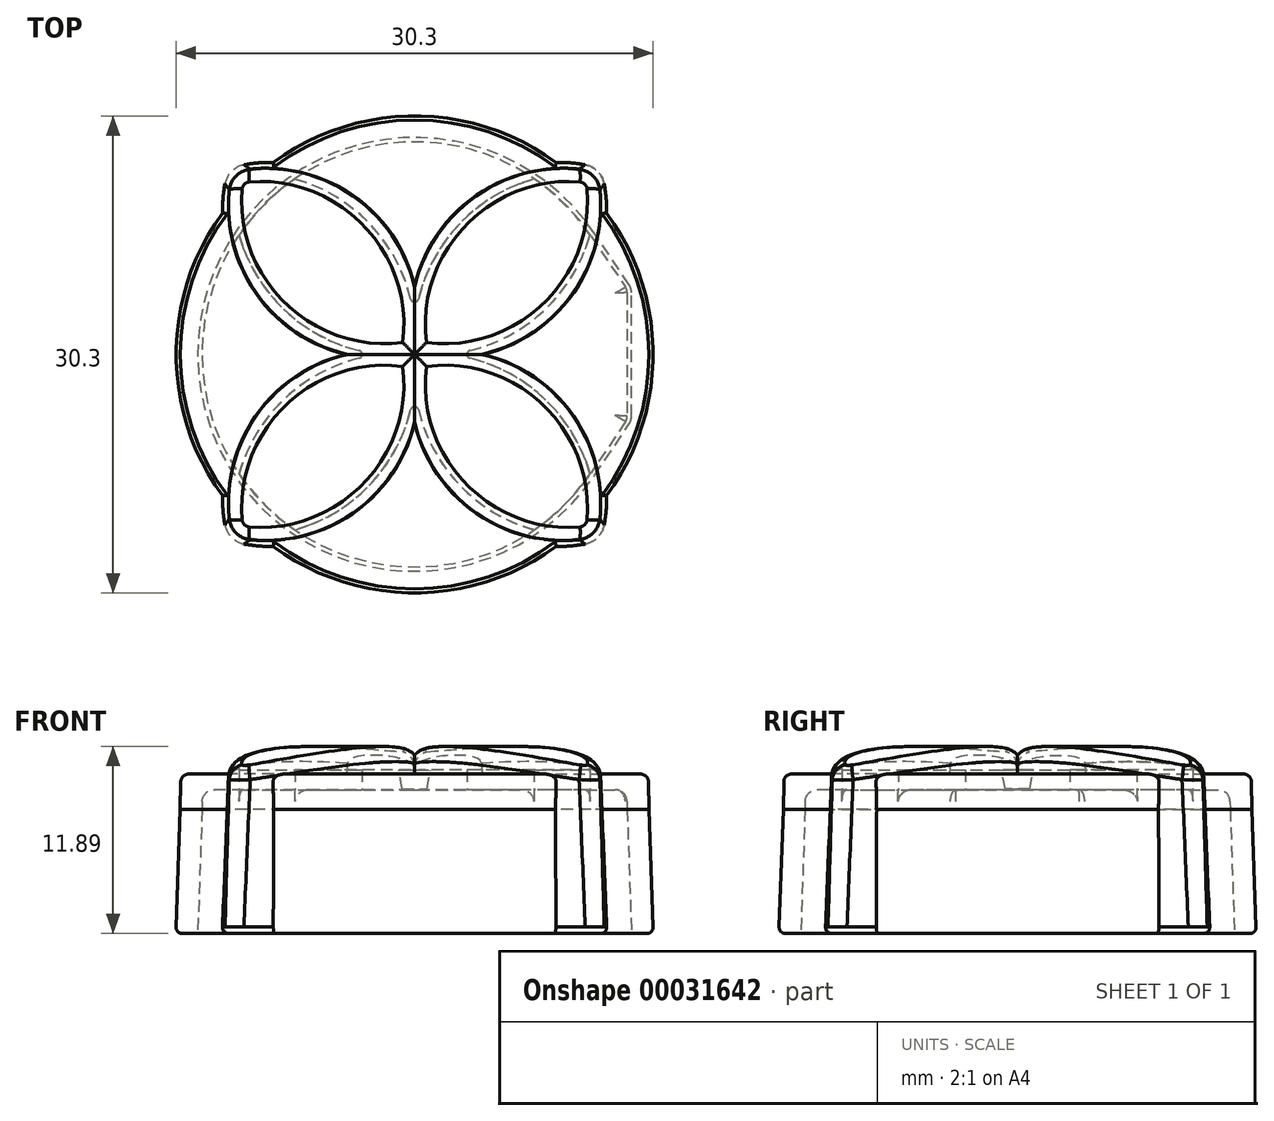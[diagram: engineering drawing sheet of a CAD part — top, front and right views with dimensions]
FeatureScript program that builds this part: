
annotation { "Feature Type Name" : "Feature", "Feature Type Description" : "" }
export const myFeature = defineFeature(function(context is Context, id is Id, definition is map)
    precondition{}
    {
        {
            var Q0;
            Q0=qCreatedBy(makeId("Top.planeOp"),FACE);
            cPlane(context, id + "F0", {"entities" : qUnion([Q0]), "cplaneType" : CPlaneType.OFFSET, "offset" : 8.73 * mm, "width" : 150 * mm, "height" : 150 * mm});
        }
        {
            var Q0;
            Q0=qCreatedBy(id+"F0.planeOp",FACE);
            var sketch = newSketch(context, id + "F1", { "sketchPlane" : qUnion([Q0])});
            skCircle(sketch, "E0", {"center": v(0, 0) * mm, "radius": 12.38 * mm});
            skCircle(sketch, "E1", {"center": v(0, 0) * mm, "radius": 13.38 * mm});
            skLineSegment(sketch, "E2.bottom", {"start": v(12.37, 4.08) * mm, "end": v(13.37, 4.08) * mm});
            skLineSegment(sketch, "E2.top", {"start": v(12.37, -4.07) * mm, "end": v(13.37, -4.07) * mm});
            skLineSegment(sketch, "E2.left", {"start": v(12.37, 3.91) * mm, "end": v(12.37, -3.91) * mm});
            skLineSegment(sketch, "E2.right", {"start": v(13.37, 3.92) * mm, "end": v(13.37, -3.92) * mm});
            skLineSegment(sketch, "E3", {"start": v(12.28, 4.2) * mm, "end": v(9.95, 7.35) * mm});
            skLineSegment(sketch, "E4", {"start": v(13.3, 4.2) * mm, "end": v(11.1, 7.46) * mm});
            skLineSegment(sketch, "E5", {"start": v(12.28, -4.2) * mm, "end": v(9.95, -7.35) * mm});
            skLineSegment(sketch, "E6", {"start": v(13.3, -4.2) * mm, "end": v(11.1, -7.46) * mm});
            skPoint(sketch, "E7.visualSharp", {"position": v(13.37, 4.08) * mm});
            skArc(sketch, "E7.filletArc", {"start": v(13.37, 3.92) * mm, "mid": v(13.35, 4.07) * mm, "end": v(13.3, 4.2) * mm});
            skPoint(sketch, "E8.visualSharp", {"position": v(13.37, -4.07) * mm});
            skArc(sketch, "E8.filletArc", {"start": v(13.3, -4.2) * mm, "mid": v(13.35, -4.07) * mm, "end": v(13.38, -3.92) * mm});
            skPoint(sketch, "E9.visualSharp", {"position": v(12.37, -4.07) * mm});
            skArc(sketch, "E9.filletArc", {"start": v(12.28, -4.2) * mm, "mid": v(12.35, -4.07) * mm, "end": v(12.38, -3.91) * mm});
            skPoint(sketch, "E10.visualSharp", {"position": v(12.37, 4.08) * mm});
            skArc(sketch, "E10.filletArc", {"start": v(12.38, 3.91) * mm, "mid": v(12.35, 4.07) * mm, "end": v(12.28, 4.2) * mm});
            skCircle(sketch, "E11.0", {"center": v(0, 0) * mm, "radius": 13.5 * mm});
            skLineSegment(sketch, "E12.0", {"start": v(13.4, 4.27) * mm, "end": v(11.2, 7.53) * mm});
            skArc(sketch, "E13.0", {"start": v(13.5, 3.92) * mm, "mid": v(13.47, 4.1) * mm, "end": v(13.4, 4.27) * mm});
            skLineSegment(sketch, "E14.0", {"start": v(13.5, 3.92) * mm, "end": v(13.5, -3.92) * mm});
            skArc(sketch, "E15.0", {"start": v(13.4, -4.27) * mm, "mid": v(13.47, -4.1) * mm, "end": v(13.5, -3.92) * mm});
            skLineSegment(sketch, "E16.0", {"start": v(13.4, -4.27) * mm, "end": v(11.2, -7.53) * mm});
            skCircle(sketch, "E17", {"center": v(0, 0) * mm, "radius": 14.88 * mm});
            skSolve(sketch);
        }
        {
            var Q0;
            {var subQ6=sQuery(id+"F1.wireOp",EDGE,"E12.0");Q0=makeQuery(id+"F1.imprint","IMPRINT",FACE,{"disambiguationData":[TD([[makeQuery(id+"F1.imprint","IMPRINT",EDGE,{"derivedFrom":subQ6}),-1.0]])]});}
            var Q1;
            {var subQ0=sQuery(id+"F1.wireOp",EDGE,"E0");var subQ3=makeQuery(id+"F1.imprint","INTERSECT",VERTEX,{"derivedFrom":[subQ0,sQuery(id+"F1.wireOp",EDGE,"E3")]});Q1=makeQuery(id+"F1.imprint","IMPRINT",FACE,{"disambiguationData":[TD([[makeQuery(id+"F1.imprint","IMPRINT",EDGE,{"disambiguationData":[TD([[subQ3,1.0]])],"derivedFrom":subQ0}),1.0]])]});}
            var Q2;
            {var subQ5=sQuery(id+"F1.wireOp",EDGE,"E4");var subQ7=sQuery(id+"F1.wireOp",EDGE,"E1");var subQ9=makeQuery(id+"F1.imprint","INTERSECT",VERTEX,{"derivedFrom":[subQ7,subQ5]});Q2=makeQuery(id+"F1.imprint","IMPRINT",FACE,{"disambiguationData":[TD([[makeQuery(id+"F1.imprint","IMPRINT",EDGE,{"disambiguationData":[TD([[subQ9,-1.0]])],"derivedFrom":subQ7}),-1.0]])]});}
            var Q3;
            {var subQ1=sQuery(id+"F1.wireOp",EDGE,"E3");Q3=makeQuery(id+"F1.imprint","IMPRINT",FACE,{"disambiguationData":[TD([[makeQuery(id+"F1.imprint","IMPRINT",EDGE,{"derivedFrom":subQ1}),-1.0]])]});}
            var Q4;
            {var subQ1=sQuery(id+"F1.wireOp",EDGE,"E3");Q4=makeQuery(id+"F1.imprint","IMPRINT",FACE,{"disambiguationData":[TD([[makeQuery(id+"F1.imprint","IMPRINT",EDGE,{"derivedFrom":subQ1}),1.0]])]});}
            var Q5;
            {var subQ3=sQuery(id+"F1.wireOp",EDGE,"E2.bottom");var subQ5=sQuery(id+"F1.wireOp",EDGE,"E7.filletArc");var subQ6=makeQuery(id+"F1.imprint","INTERSECT",VERTEX,{"derivedFrom":[subQ3,subQ5]});Q5=makeQuery(id+"F1.imprint","IMPRINT",FACE,{"disambiguationData":[TD([[makeQuery(id+"F1.imprint","IMPRINT",EDGE,{"disambiguationData":[TD([[subQ6,1.0]])],"derivedFrom":subQ3}),1.0]])]});}
            var Q6;
            {var subQ3=sQuery(id+"F1.wireOp",EDGE,"E2.bottom");var subQ5=sQuery(id+"F1.wireOp",EDGE,"E7.filletArc");var subQ6=makeQuery(id+"F1.imprint","INTERSECT",VERTEX,{"derivedFrom":[subQ3,subQ5]});Q6=makeQuery(id+"F1.imprint","IMPRINT",FACE,{"disambiguationData":[TD([[makeQuery(id+"F1.imprint","IMPRINT",EDGE,{"disambiguationData":[TD([[subQ6,1.0]])],"derivedFrom":subQ3}),-1.0]])]});}
            var Q7;
            {var subQ3=sQuery(id+"F1.wireOp",EDGE,"E2.bottom");var subQ5=sQuery(id+"F1.wireOp",EDGE,"E1");var subQ7=makeQuery(id+"F1.imprint","INTERSECT",VERTEX,{"derivedFrom":[subQ5,subQ3]});Q7=makeQuery(id+"F1.imprint","IMPRINT",FACE,{"disambiguationData":[TD([[makeQuery(id+"F1.imprint","IMPRINT",EDGE,{"disambiguationData":[TD([[subQ7,1.0]])],"derivedFrom":subQ5}),-1.0]])]});}
            var Q8;
            {var subQ1=sQuery(id+"F1.wireOp",EDGE,"E4");var subQ5=sQuery(id+"F1.wireOp",EDGE,"E1");var subQ6=makeQuery(id+"F1.imprint","INTERSECT",VERTEX,{"derivedFrom":[subQ5,subQ1]});Q8=makeQuery(id+"F1.imprint","IMPRINT",FACE,{"disambiguationData":[TD([[makeQuery(id+"F1.imprint","IMPRINT",EDGE,{"disambiguationData":[TD([[subQ6,1.0]])],"derivedFrom":subQ5}),-1.0]])]});}
            var Q9;
            {var subQ4=sQuery(id+"F1.wireOp",EDGE,"E12.0");Q9=makeQuery(id+"F1.imprint","IMPRINT",FACE,{"disambiguationData":[TD([[makeQuery(id+"F1.imprint","IMPRINT",EDGE,{"derivedFrom":subQ4}),1.0]])]});}
            var Q10;
            {var subQ2=sQuery(id+"F1.wireOp",EDGE,"E2.right");var subQ5=makeQuery(id+"F1.imprint","INTERSECT",VERTEX,{"derivedFrom":[sQuery(id+"F1.wireOp",EDGE,"E1"),subQ2]});Q10=makeQuery(id+"F1.imprint","IMPRINT",FACE,{"disambiguationData":[TD([[makeQuery(id+"F1.imprint","IMPRINT",EDGE,{"disambiguationData":[TD([[subQ5,1.0]])],"derivedFrom":subQ2}),1.0]])]});}
            var Q11;
            {var subQ1=sQuery(id+"F1.wireOp",EDGE,"E5");Q11=makeQuery(id+"F1.imprint","IMPRINT",FACE,{"disambiguationData":[TD([[makeQuery(id+"F1.imprint","IMPRINT",EDGE,{"derivedFrom":subQ1}),-1.0]])]});}
            var Q12;
            {var subQ3=sQuery(id+"F1.wireOp",EDGE,"E2.top");var subQ5=sQuery(id+"F1.wireOp",EDGE,"E8.filletArc");var subQ6=makeQuery(id+"F1.imprint","INTERSECT",VERTEX,{"derivedFrom":[subQ3,subQ5]});Q12=makeQuery(id+"F1.imprint","IMPRINT",FACE,{"disambiguationData":[TD([[makeQuery(id+"F1.imprint","IMPRINT",EDGE,{"disambiguationData":[TD([[subQ6,1.0]])],"derivedFrom":subQ3}),1.0]])]});}
            var Q13;
            {var subQ3=sQuery(id+"F1.wireOp",EDGE,"E2.top");var subQ5=sQuery(id+"F1.wireOp",EDGE,"E1");var subQ7=makeQuery(id+"F1.imprint","INTERSECT",VERTEX,{"derivedFrom":[subQ5,subQ3]});Q13=makeQuery(id+"F1.imprint","IMPRINT",FACE,{"disambiguationData":[TD([[makeQuery(id+"F1.imprint","IMPRINT",EDGE,{"disambiguationData":[TD([[subQ7,-1.0]])],"derivedFrom":subQ5}),-1.0]])]});}
            var Q14;
            {var subQ0=sQuery(id+"F1.wireOp",EDGE,"E15.0");Q14=makeQuery(id+"F1.imprint","IMPRINT",FACE,{"disambiguationData":[TD([[makeQuery(id+"F1.imprint","IMPRINT",EDGE,{"derivedFrom":subQ0}),1.0]])]});}
            var Q15;
            {var subQ1=sQuery(id+"F1.wireOp",EDGE,"E6");var subQ5=sQuery(id+"F1.wireOp",EDGE,"E1");var subQ6=makeQuery(id+"F1.imprint","INTERSECT",VERTEX,{"derivedFrom":[subQ5,subQ1]});Q15=makeQuery(id+"F1.imprint","IMPRINT",FACE,{"disambiguationData":[TD([[makeQuery(id+"F1.imprint","IMPRINT",EDGE,{"disambiguationData":[TD([[subQ6,-1.0]])],"derivedFrom":subQ5}),-1.0]])]});}
            var Q16;
            {var subQ3=sQuery(id+"F1.wireOp",EDGE,"E2.top");var subQ5=sQuery(id+"F1.wireOp",EDGE,"E8.filletArc");var subQ6=makeQuery(id+"F1.imprint","INTERSECT",VERTEX,{"derivedFrom":[subQ3,subQ5]});Q16=makeQuery(id+"F1.imprint","IMPRINT",FACE,{"disambiguationData":[TD([[makeQuery(id+"F1.imprint","IMPRINT",EDGE,{"disambiguationData":[TD([[subQ6,1.0]])],"derivedFrom":subQ3}),-1.0]])]});}
            extrude(context, id + "F2", {"entities" : qUnion([Q0, Q1, Q2, Q3, Q4, Q5, Q6, Q7, Q8, Q9, Q10, Q11, Q12, Q13, Q14, Q15, Q16]), "depth" : 2.25 * mm, "hasDraft" : true, "draftAngle" : 1 * degree, "draftPullDirection" : true});
        }
        {
            var Q0;
            {var subQ6=sQuery(id+"F1.wireOp",EDGE,"E12.0");Q0=makeQuery(id+"F1.imprint","IMPRINT",FACE,{"disambiguationData":[TD([[makeQuery(id+"F1.imprint","IMPRINT",EDGE,{"derivedFrom":subQ6}),-1.0]])]});}
            var Q1;
            {var subQ1=sQuery(id+"F1.wireOp",EDGE,"E3");Q1=makeQuery(id+"F1.imprint","IMPRINT",FACE,{"disambiguationData":[TD([[makeQuery(id+"F1.imprint","IMPRINT",EDGE,{"derivedFrom":subQ1}),-1.0]])]});}
            var Q2;
            {var subQ5=sQuery(id+"F1.wireOp",EDGE,"E4");var subQ7=sQuery(id+"F1.wireOp",EDGE,"E1");var subQ9=makeQuery(id+"F1.imprint","INTERSECT",VERTEX,{"derivedFrom":[subQ7,subQ5]});Q2=makeQuery(id+"F1.imprint","IMPRINT",FACE,{"disambiguationData":[TD([[makeQuery(id+"F1.imprint","IMPRINT",EDGE,{"disambiguationData":[TD([[subQ9,-1.0]])],"derivedFrom":subQ7}),-1.0]])]});}
            var Q3;
            {var subQ1=sQuery(id+"F1.wireOp",EDGE,"E3");Q3=makeQuery(id+"F1.imprint","IMPRINT",FACE,{"disambiguationData":[TD([[makeQuery(id+"F1.imprint","IMPRINT",EDGE,{"derivedFrom":subQ1}),1.0]])]});}
            var Q4;
            {var subQ0=sQuery(id+"F1.wireOp",EDGE,"E0");var subQ3=makeQuery(id+"F1.imprint","INTERSECT",VERTEX,{"derivedFrom":[subQ0,sQuery(id+"F1.wireOp",EDGE,"E3")]});Q4=makeQuery(id+"F1.imprint","IMPRINT",FACE,{"disambiguationData":[TD([[makeQuery(id+"F1.imprint","IMPRINT",EDGE,{"disambiguationData":[TD([[subQ3,1.0]])],"derivedFrom":subQ0}),1.0]])]});}
            var Q5;
            {var subQ1=sQuery(id+"F1.wireOp",EDGE,"E4");var subQ5=sQuery(id+"F1.wireOp",EDGE,"E1");var subQ6=makeQuery(id+"F1.imprint","INTERSECT",VERTEX,{"derivedFrom":[subQ5,subQ1]});Q5=makeQuery(id+"F1.imprint","IMPRINT",FACE,{"disambiguationData":[TD([[makeQuery(id+"F1.imprint","IMPRINT",EDGE,{"disambiguationData":[TD([[subQ6,1.0]])],"derivedFrom":subQ5}),-1.0]])]});}
            var Q6;
            {var subQ4=sQuery(id+"F1.wireOp",EDGE,"E12.0");Q6=makeQuery(id+"F1.imprint","IMPRINT",FACE,{"disambiguationData":[TD([[makeQuery(id+"F1.imprint","IMPRINT",EDGE,{"derivedFrom":subQ4}),1.0]])]});}
            var Q7;
            {var subQ3=sQuery(id+"F1.wireOp",EDGE,"E2.bottom");var subQ5=sQuery(id+"F1.wireOp",EDGE,"E7.filletArc");var subQ6=makeQuery(id+"F1.imprint","INTERSECT",VERTEX,{"derivedFrom":[subQ3,subQ5]});Q7=makeQuery(id+"F1.imprint","IMPRINT",FACE,{"disambiguationData":[TD([[makeQuery(id+"F1.imprint","IMPRINT",EDGE,{"disambiguationData":[TD([[subQ6,1.0]])],"derivedFrom":subQ3}),1.0]])]});}
            var Q8;
            {var subQ3=sQuery(id+"F1.wireOp",EDGE,"E2.bottom");var subQ5=sQuery(id+"F1.wireOp",EDGE,"E7.filletArc");var subQ6=makeQuery(id+"F1.imprint","INTERSECT",VERTEX,{"derivedFrom":[subQ3,subQ5]});Q8=makeQuery(id+"F1.imprint","IMPRINT",FACE,{"disambiguationData":[TD([[makeQuery(id+"F1.imprint","IMPRINT",EDGE,{"disambiguationData":[TD([[subQ6,1.0]])],"derivedFrom":subQ3}),-1.0]])]});}
            var Q9;
            {var subQ3=sQuery(id+"F1.wireOp",EDGE,"E2.bottom");var subQ5=sQuery(id+"F1.wireOp",EDGE,"E1");var subQ7=makeQuery(id+"F1.imprint","INTERSECT",VERTEX,{"derivedFrom":[subQ5,subQ3]});Q9=makeQuery(id+"F1.imprint","IMPRINT",FACE,{"disambiguationData":[TD([[makeQuery(id+"F1.imprint","IMPRINT",EDGE,{"disambiguationData":[TD([[subQ7,1.0]])],"derivedFrom":subQ5}),-1.0]])]});}
            var Q10;
            {var subQ2=sQuery(id+"F1.wireOp",EDGE,"E2.right");var subQ5=makeQuery(id+"F1.imprint","INTERSECT",VERTEX,{"derivedFrom":[sQuery(id+"F1.wireOp",EDGE,"E1"),subQ2]});Q10=makeQuery(id+"F1.imprint","IMPRINT",FACE,{"disambiguationData":[TD([[makeQuery(id+"F1.imprint","IMPRINT",EDGE,{"disambiguationData":[TD([[subQ5,1.0]])],"derivedFrom":subQ2}),1.0]])]});}
            var Q11;
            {var subQ1=sQuery(id+"F1.wireOp",EDGE,"E5");Q11=makeQuery(id+"F1.imprint","IMPRINT",FACE,{"disambiguationData":[TD([[makeQuery(id+"F1.imprint","IMPRINT",EDGE,{"derivedFrom":subQ1}),-1.0]])]});}
            var Q12;
            {var subQ3=sQuery(id+"F1.wireOp",EDGE,"E2.top");var subQ5=sQuery(id+"F1.wireOp",EDGE,"E8.filletArc");var subQ6=makeQuery(id+"F1.imprint","INTERSECT",VERTEX,{"derivedFrom":[subQ3,subQ5]});Q12=makeQuery(id+"F1.imprint","IMPRINT",FACE,{"disambiguationData":[TD([[makeQuery(id+"F1.imprint","IMPRINT",EDGE,{"disambiguationData":[TD([[subQ6,1.0]])],"derivedFrom":subQ3}),1.0]])]});}
            var Q13;
            {var subQ3=sQuery(id+"F1.wireOp",EDGE,"E2.top");var subQ5=sQuery(id+"F1.wireOp",EDGE,"E1");var subQ7=makeQuery(id+"F1.imprint","INTERSECT",VERTEX,{"derivedFrom":[subQ5,subQ3]});Q13=makeQuery(id+"F1.imprint","IMPRINT",FACE,{"disambiguationData":[TD([[makeQuery(id+"F1.imprint","IMPRINT",EDGE,{"disambiguationData":[TD([[subQ7,-1.0]])],"derivedFrom":subQ5}),-1.0]])]});}
            var Q14;
            {var subQ0=sQuery(id+"F1.wireOp",EDGE,"E15.0");Q14=makeQuery(id+"F1.imprint","IMPRINT",FACE,{"disambiguationData":[TD([[makeQuery(id+"F1.imprint","IMPRINT",EDGE,{"derivedFrom":subQ0}),1.0]])]});}
            var Q15;
            {var subQ3=sQuery(id+"F1.wireOp",EDGE,"E2.top");var subQ5=sQuery(id+"F1.wireOp",EDGE,"E8.filletArc");var subQ6=makeQuery(id+"F1.imprint","INTERSECT",VERTEX,{"derivedFrom":[subQ3,subQ5]});Q15=makeQuery(id+"F1.imprint","IMPRINT",FACE,{"disambiguationData":[TD([[makeQuery(id+"F1.imprint","IMPRINT",EDGE,{"disambiguationData":[TD([[subQ6,1.0]])],"derivedFrom":subQ3}),-1.0]])]});}
            var Q16;
            {var subQ1=sQuery(id+"F1.wireOp",EDGE,"E6");var subQ5=sQuery(id+"F1.wireOp",EDGE,"E1");var subQ6=makeQuery(id+"F1.imprint","INTERSECT",VERTEX,{"derivedFrom":[subQ5,subQ1]});Q16=makeQuery(id+"F1.imprint","IMPRINT",FACE,{"disambiguationData":[TD([[makeQuery(id+"F1.imprint","IMPRINT",EDGE,{"disambiguationData":[TD([[subQ6,-1.0]])],"derivedFrom":subQ5}),-1.0]])]});}
            extrude(context, id + "F3", {"entities" : qUnion([Q0, Q1, Q2, Q3, Q4, Q5, Q6, Q7, Q8, Q9, Q10, Q11, Q12, Q13, Q14, Q15, Q16]), "operationType" : NewBodyOperationType.ADD, "oppositeDirection" : true, "depth" : 7.88 * mm, "hasDraft" : true, "draftAngle" : 2 * degree});
        }
        {
            var Q0;
            Q0=qCreatedBy(makeId("Top.planeOp"),FACE);
            var sketch = newSketch(context, id + "F4", { "sketchPlane" : qUnion([Q0])});
            skLineSegment(sketch, "E18", {"start": v(0, 0) * mm, "end": v(0, 19.92) * mm, "construction": true});
            skLineSegment(sketch, "E19", {"start": v(0, 0) * mm, "end": v(17.2, 17.2) * mm, "construction": true});
            skArc(sketch, "E20", {"start": v(11.84, 11.84) * mm, "mid": v(2.38, 9.47) * mm, "end": v(0, 0) * mm});
            skArc(sketch, "E21.0.MirrorCS", {"start": v(11.84, 11.84) * mm, "mid": v(9.47, 2.38) * mm, "end": v(0, 0) * mm});
            skPoint(sketch, "E22.center", {"position": v(0, 0) * mm});
            skLineSegment(sketch, "E22.anchor1", {"start": v(0, 0) * mm, "end": v(0, 0) * mm});
            skLineSegment(sketch, "E22.anchor2", {"start": v(0, 0) * mm, "end": v(21.18, 0) * mm, "construction": true});
            skSolve(sketch);
        }
        {
            var Q0;
            Q0=qCreatedBy(makeId("Top.planeOp"),FACE);
            cPlane(context, id + "F5", {"entities" : qUnion([Q0]), "cplaneType" : CPlaneType.OFFSET, "offset" : 13.98 * mm, "width" : 150 * mm, "height" : 150 * mm});
        }
        {
            var Q0;
            Q0=qCreatedBy(id+"F5.planeOp",FACE);
            var sketch = newSketch(context, id + "F6", { "sketchPlane" : qUnion([Q0])});
            skLineSegment(sketch, "E23", {"start": v(0, 0) * mm, "end": v(0, 1.45) * mm, "construction": true});
            skLineSegment(sketch, "E24", {"start": v(0, 0) * mm, "end": v(22.98, 22.98) * mm, "construction": true});
            skArc(sketch, "E25", {"start": v(11.5, 11.5) * mm, "mid": v(2.63, 8.86) * mm, "end": v(0, 0) * mm});
            skArc(sketch, "E26", {"start": v(11.84, 11.84) * mm, "mid": v(2.71, 9.13) * mm, "end": v(0, 0) * mm, "construction": true});
            skArc(sketch, "E27.0.MirrorCS", {"start": v(11.5, 11.5) * mm, "mid": v(8.86, 2.63) * mm, "end": v(0, 0) * mm});
            skSolve(sketch);
        }
        {
            var Q1;
            Q1=makeQuery(id+"F4.imprint","IMPRINT",FACE,{"disambiguationData":[TD([[makeQuery(id+"F4.imprint","IMPRINT",EDGE,{"derivedFrom":sQuery(id+"F4.wireOp",EDGE,"E20")}),1.0]])]});
            var Q2;
            Q2=makeQuery(id+"F6.imprint","IMPRINT",FACE,{"disambiguationData":[TD([[makeQuery(id+"F6.imprint","IMPRINT",EDGE,{"derivedFrom":sQuery(id+"F6.wireOp",EDGE,"E25")}),1.0]])]});
            loft(context, id + "F7", {"sheetProfilesArray" : [{ "sheetProfileEntities" : qUnion([Q1]) }, { "sheetProfileEntities" : qUnion([Q2]) }]});
        }
        {
            var Q0;
            Q0=qCreatedBy(makeId("Front.planeOp"),FACE);
            var Q1;
            Q1=qCreatedBy(makeId("Right.planeOp"),FACE);
            cPlane(context, id + "F8", {"entities" : qUnion([Q0, Q1]), "cplaneType" : CPlaneType.MID_PLANE, "offset" : 150 * mm, "flipAlignment" : true, "width" : 150 * mm, "height" : 150 * mm});
        }
        {
            var Q0;
            Q0=qCreatedBy(id+"F8.planeOp",FACE);
            var sketch = newSketch(context, id + "F9", { "sketchPlane" : qUnion([Q0])});
            skLineSegment(sketch, "E28", {"start": v(0, 0) * mm, "end": v(0, 14) * mm});
            skLineSegment(sketch, "E29", {"start": v(0, 0.85) * mm, "end": v(16.75, 0.85) * mm});
            skLineSegment(sketch, "E30", {"start": v(0, 11.23) * mm, "end": v(23.83, 11.23) * mm, "construction": true});
            skLineSegment(sketch, "E31", {"start": v(16.75, 0.85) * mm, "end": v(16.37, 11.24) * mm});
            skLineSegment(sketch, "E32", {"start": v(16.75, 0.85) * mm, "end": v(16.75, 14) * mm});
            skLineSegment(sketch, "E33", {"start": v(0, 14) * mm, "end": v(16.75, 14) * mm});
            skLineSegment(sketch, "E34", {"start": v(16.75, 0.85) * mm, "end": v(16.75, -1.44) * mm});
            skLineSegment(sketch, "E35", {"start": v(16.75, -1.44) * mm, "end": v(0, -1.44) * mm});
            skLineSegment(sketch, "E36", {"start": v(0, -1.44) * mm, "end": v(0, 0.85) * mm});
            skArc(sketch, "E37", {"start": v(16.38, 11.24) * mm, "mid": v(8.24, 12.67) * mm, "end": v(0, 12.23) * mm});
            skLineSegment(sketch, "E38", {"start": v(0, 12.73) * mm, "end": v(27.33, 12.73) * mm, "construction": true});
            skSolve(sketch);
        }
        {
            var Q0;
            Q0=makeQuery(id+"F9.imprint","IMPRINT",FACE,{"disambiguationData":[TD([[makeQuery(id+"F9.imprint","IMPRINT",EDGE,{"derivedFrom":sQuery(id+"F9.wireOp",EDGE,"E31")}),-1.0]])]});
            var Q1;
            {var subQ2=sQuery(id+"F9.wireOp",EDGE,"E29");Q1=makeQuery(id+"F9.imprint","IMPRINT",FACE,{"disambiguationData":[TD([[makeQuery(id+"F9.imprint","IMPRINT",EDGE,{"derivedFrom":subQ2}),-1.0]])]});}
            extrude(context, id + "F10", {"entities" : qUnion([Q0, Q1]), "operationType" : NewBodyOperationType.REMOVE, "endBound" : BoundingType.SYMMETRIC, "oppositeDirection" : true, "depth" : 12 * mm});
        }
        {
            var Q0;
            {var subQ0=sQuery(id+"F4.wireOp",EDGE,"E20");var subQ1=sQuery(id+"F4.wireOp",EDGE,"E21.0.MirrorCS");var subQ2=sQuery(id+"F6.wireOp",EDGE,"E25");var subQ3=sQuery(id+"F6.wireOp",EDGE,"E27.0.MirrorCS");Q0=makeQuery(id+"F7.opLoft","SWEPT_EDGE",EDGE,{"disambiguationData":[OSD([subQ0,subQ1,subQ2,subQ3]),TDD([makeQuery(id+"F4.imprint","INTERSECT",VERTEX,{"disambiguationData":[OD(0.0)],"derivedFrom":[subQ0,subQ1]}),makeQuery(id+"F6.imprint","INTERSECT",VERTEX,{"disambiguationData":[OD(0.0)],"derivedFrom":[subQ2,subQ3]})])]});}
            fillet(context, id + "F11", {"entities" : qUnion([Q0]), "radius" : 1.5 * mm, "tangentPropagation" : true, "allowEdgeOverflow" : false});
        }
        {
            var Q0;
            {var subQ0=sQuery(id+"F4.wireOp",EDGE,"E20");var subQ1=sQuery(id+"F4.wireOp",EDGE,"E21.0.MirrorCS");var subQ2=sQuery(id+"F6.wireOp",EDGE,"E25");var subQ3=sQuery(id+"F6.wireOp",EDGE,"E27.0.MirrorCS");Q0=makeQuery(id+"F10.boolean.opBoolean","INTERSECT",EDGE,{"derivedFrom":[makeQuery(id+"F7.opLoft","SWEPT_FACE",FACE,{"disambiguationData":[OSD([subQ0,subQ1,subQ2,subQ3]),TDD([makeQuery(id+"F4.imprint","INTERSECT",VERTEX,{"disambiguationData":[OD(0.0)],"derivedFrom":[subQ0,subQ1]}),makeQuery(id+"F4.imprint","INTERSECT",VERTEX,{"disambiguationData":[OD(1.0)],"derivedFrom":[subQ0,subQ1]}),makeQuery(id+"F4.imprint","IMPRINT",EDGE,{"derivedFrom":subQ1}),makeQuery(id+"F6.imprint","INTERSECT",VERTEX,{"disambiguationData":[OD(0.0)],"derivedFrom":[subQ2,subQ3]}),makeQuery(id+"F6.imprint","INTERSECT",VERTEX,{"disambiguationData":[OD(1.0)],"derivedFrom":[subQ2,subQ3]}),makeQuery(id+"F6.imprint","IMPRINT",EDGE,{"derivedFrom":subQ3})])]}),makeQuery(id+"F10.opExtrude","SWEPT_FACE",FACE,{"disambiguationData":[OSD([sQuery(id+"F9.wireOp",EDGE,"E37")])]})]});}
            fillet(context, id + "F12", {"entities" : qUnion([Q0]), "radius" : 1 * mm, "tangentPropagation" : true, "allowEdgeOverflow" : false});
        }
        {
            var Q0;
            Q0=makeQuery(id+"F7.opLoft","SWEPT_BODY",BODY,{"disambiguationData":[OSD([makeQuery(id+"F4.imprint","IMPRINT",FACE,{"disambiguationData":[TD([[makeQuery(id+"F4.imprint","IMPRINT",EDGE,{"derivedFrom":sQuery(id+"F4.wireOp",EDGE,"E20")}),1.0]])]}),makeQuery(id+"F6.imprint","IMPRINT",FACE,{"disambiguationData":[TD([[makeQuery(id+"F6.imprint","IMPRINT",EDGE,{"derivedFrom":sQuery(id+"F6.wireOp",EDGE,"E25")}),1.0]])]})])]});
            var Q1;
            Q1=sQuery(id+"F9.wireOp",EDGE,"E28");
            circularPattern(context, id + "F13", {"operationType" : NewBodyOperationType.ADD, "entities" : qUnion([Q0]), "axis" : qUnion([Q1]), "angle" : 90 * degree, "instanceCount" : round(4)});
        }
        {
            var Q0;
            {var subQ0=sQuery(id+"F1.wireOp",EDGE,"E0");var subQ3=makeQuery(id+"F1.imprint","INTERSECT",VERTEX,{"derivedFrom":[subQ0,sQuery(id+"F1.wireOp",EDGE,"E3")]});Q0=makeQuery(id+"F1.imprint","IMPRINT",FACE,{"disambiguationData":[TD([[makeQuery(id+"F1.imprint","IMPRINT",EDGE,{"disambiguationData":[TD([[subQ3,1.0]])],"derivedFrom":subQ0}),1.0]])]});}
            var Q1;
            {var subQ1=sQuery(id+"F1.wireOp",EDGE,"E3");Q1=makeQuery(id+"F1.imprint","IMPRINT",FACE,{"disambiguationData":[TD([[makeQuery(id+"F1.imprint","IMPRINT",EDGE,{"derivedFrom":subQ1}),-1.0]])]});}
            var Q2;
            {var subQ5=sQuery(id+"F1.wireOp",EDGE,"E4");var subQ7=sQuery(id+"F1.wireOp",EDGE,"E1");var subQ9=makeQuery(id+"F1.imprint","INTERSECT",VERTEX,{"derivedFrom":[subQ7,subQ5]});Q2=makeQuery(id+"F1.imprint","IMPRINT",FACE,{"disambiguationData":[TD([[makeQuery(id+"F1.imprint","IMPRINT",EDGE,{"disambiguationData":[TD([[subQ9,-1.0]])],"derivedFrom":subQ7}),-1.0]])]});}
            var Q3;
            {var subQ4=sQuery(id+"F1.wireOp",EDGE,"E12.0");Q3=makeQuery(id+"F1.imprint","IMPRINT",FACE,{"disambiguationData":[TD([[makeQuery(id+"F1.imprint","IMPRINT",EDGE,{"derivedFrom":subQ4}),1.0]])]});}
            var Q4;
            {var subQ3=sQuery(id+"F1.wireOp",EDGE,"E2.bottom");var subQ5=sQuery(id+"F1.wireOp",EDGE,"E7.filletArc");var subQ6=makeQuery(id+"F1.imprint","INTERSECT",VERTEX,{"derivedFrom":[subQ3,subQ5]});Q4=makeQuery(id+"F1.imprint","IMPRINT",FACE,{"disambiguationData":[TD([[makeQuery(id+"F1.imprint","IMPRINT",EDGE,{"disambiguationData":[TD([[subQ6,1.0]])],"derivedFrom":subQ3}),1.0]])]});}
            var Q5;
            {var subQ3=sQuery(id+"F1.wireOp",EDGE,"E2.bottom");var subQ5=sQuery(id+"F1.wireOp",EDGE,"E7.filletArc");var subQ6=makeQuery(id+"F1.imprint","INTERSECT",VERTEX,{"derivedFrom":[subQ3,subQ5]});Q5=makeQuery(id+"F1.imprint","IMPRINT",FACE,{"disambiguationData":[TD([[makeQuery(id+"F1.imprint","IMPRINT",EDGE,{"disambiguationData":[TD([[subQ6,1.0]])],"derivedFrom":subQ3}),-1.0]])]});}
            var Q6;
            {var subQ1=sQuery(id+"F1.wireOp",EDGE,"E3");Q6=makeQuery(id+"F1.imprint","IMPRINT",FACE,{"disambiguationData":[TD([[makeQuery(id+"F1.imprint","IMPRINT",EDGE,{"derivedFrom":subQ1}),1.0]])]});}
            var Q7;
            {var subQ3=sQuery(id+"F1.wireOp",EDGE,"E2.bottom");var subQ5=sQuery(id+"F1.wireOp",EDGE,"E1");var subQ7=makeQuery(id+"F1.imprint","INTERSECT",VERTEX,{"derivedFrom":[subQ5,subQ3]});Q7=makeQuery(id+"F1.imprint","IMPRINT",FACE,{"disambiguationData":[TD([[makeQuery(id+"F1.imprint","IMPRINT",EDGE,{"disambiguationData":[TD([[subQ7,1.0]])],"derivedFrom":subQ5}),-1.0]])]});}
            var Q8;
            {var subQ1=sQuery(id+"F1.wireOp",EDGE,"E4");var subQ5=sQuery(id+"F1.wireOp",EDGE,"E1");var subQ6=makeQuery(id+"F1.imprint","INTERSECT",VERTEX,{"derivedFrom":[subQ5,subQ1]});Q8=makeQuery(id+"F1.imprint","IMPRINT",FACE,{"disambiguationData":[TD([[makeQuery(id+"F1.imprint","IMPRINT",EDGE,{"disambiguationData":[TD([[subQ6,1.0]])],"derivedFrom":subQ5}),-1.0]])]});}
            var Q9;
            {var subQ1=sQuery(id+"F1.wireOp",EDGE,"E5");Q9=makeQuery(id+"F1.imprint","IMPRINT",FACE,{"disambiguationData":[TD([[makeQuery(id+"F1.imprint","IMPRINT",EDGE,{"derivedFrom":subQ1}),-1.0]])]});}
            var Q10;
            {var subQ3=sQuery(id+"F1.wireOp",EDGE,"E2.top");var subQ5=sQuery(id+"F1.wireOp",EDGE,"E1");var subQ7=makeQuery(id+"F1.imprint","INTERSECT",VERTEX,{"derivedFrom":[subQ5,subQ3]});Q10=makeQuery(id+"F1.imprint","IMPRINT",FACE,{"disambiguationData":[TD([[makeQuery(id+"F1.imprint","IMPRINT",EDGE,{"disambiguationData":[TD([[subQ7,-1.0]])],"derivedFrom":subQ5}),-1.0]])]});}
            var Q11;
            {var subQ1=sQuery(id+"F1.wireOp",EDGE,"E6");var subQ5=sQuery(id+"F1.wireOp",EDGE,"E1");var subQ6=makeQuery(id+"F1.imprint","INTERSECT",VERTEX,{"derivedFrom":[subQ5,subQ1]});Q11=makeQuery(id+"F1.imprint","IMPRINT",FACE,{"disambiguationData":[TD([[makeQuery(id+"F1.imprint","IMPRINT",EDGE,{"disambiguationData":[TD([[subQ6,-1.0]])],"derivedFrom":subQ5}),-1.0]])]});}
            var Q12;
            {var subQ3=sQuery(id+"F1.wireOp",EDGE,"E2.top");var subQ5=sQuery(id+"F1.wireOp",EDGE,"E8.filletArc");var subQ6=makeQuery(id+"F1.imprint","INTERSECT",VERTEX,{"derivedFrom":[subQ3,subQ5]});Q12=makeQuery(id+"F1.imprint","IMPRINT",FACE,{"disambiguationData":[TD([[makeQuery(id+"F1.imprint","IMPRINT",EDGE,{"disambiguationData":[TD([[subQ6,1.0]])],"derivedFrom":subQ3}),-1.0]])]});}
            var Q13;
            {var subQ0=sQuery(id+"F1.wireOp",EDGE,"E15.0");Q13=makeQuery(id+"F1.imprint","IMPRINT",FACE,{"disambiguationData":[TD([[makeQuery(id+"F1.imprint","IMPRINT",EDGE,{"derivedFrom":subQ0}),1.0]])]});}
            var Q14;
            {var subQ3=sQuery(id+"F1.wireOp",EDGE,"E2.top");var subQ5=sQuery(id+"F1.wireOp",EDGE,"E8.filletArc");var subQ6=makeQuery(id+"F1.imprint","INTERSECT",VERTEX,{"derivedFrom":[subQ3,subQ5]});Q14=makeQuery(id+"F1.imprint","IMPRINT",FACE,{"disambiguationData":[TD([[makeQuery(id+"F1.imprint","IMPRINT",EDGE,{"disambiguationData":[TD([[subQ6,1.0]])],"derivedFrom":subQ3}),1.0]])]});}
            var Q15;
            {var subQ2=sQuery(id+"F1.wireOp",EDGE,"E2.right");var subQ5=makeQuery(id+"F1.imprint","INTERSECT",VERTEX,{"derivedFrom":[sQuery(id+"F1.wireOp",EDGE,"E1"),subQ2]});Q15=makeQuery(id+"F1.imprint","IMPRINT",FACE,{"disambiguationData":[TD([[makeQuery(id+"F1.imprint","IMPRINT",EDGE,{"disambiguationData":[TD([[subQ5,1.0]])],"derivedFrom":subQ2}),1.0]])]});}
            extrude(context, id + "F14", {"entities" : qUnion([Q0, Q1, Q2, Q3, Q4, Q5, Q6, Q7, Q8, Q9, Q10, Q11, Q12, Q13, Q14, Q15]), "operationType" : NewBodyOperationType.REMOVE, "depth" : 1.25 * mm, "hasDraft" : true, "draftAngle" : 1 * degree, "draftPullDirection" : true, "hasSecondDirection" : true, "secondDirectionBound" : SecondDirectionBoundingType.THROUGH_ALL, "secondDirectionOppositeDirection" : true, "secondDirectionDepth" : 25 * mm, "hasSecondDirectionDraft" : true, "secondDirectionDraftAngle" : 2 * degree});
        }
        {
            var Q0;
            Q0=makeQuery(id+"F14.boolean.opBoolean","COPY",FACE,{"disambiguationData":[OD(0.0)],"derivedFrom":makeQuery(id+"F14.opExtrude","CAP_FACE",FACE,{"disambiguationData":[OSD([sQuery(id+"F1.wireOp",EDGE,"E11.0"),sQuery(id+"F1.wireOp",EDGE,"E12.0"),sQuery(id+"F1.wireOp",EDGE,"E13.0"),sQuery(id+"F1.wireOp",EDGE,"E14.0"),sQuery(id+"F1.wireOp",EDGE,"E15.0"),sQuery(id+"F1.wireOp",EDGE,"E16.0")])],"isStart":false})});
            var sketch = newSketch(context, id + "F15", { "sketchPlane" : qUnion([Q0])});
            skLineSegment(sketch, "E39", {"start": v(0, 0) * mm, "end": v(14.5, 14.5) * mm, "construction": true});
            skPoint(sketch, "E40.center", {"position": v(0, 0) * mm});
            skLineSegment(sketch, "E41", {"start": v(-34.97, -4.74) * mm, "end": v(-34.97, -3.29) * mm, "construction": true});
            skLineSegment(sketch, "E42", {"start": v(-34.97, -4.74) * mm, "end": v(-11.99, 18.24) * mm, "construction": true});
            skArc(sketch, "E43", {"start": v(-23.48, 6.75) * mm, "mid": v(-32.33, 4.11) * mm, "end": v(-34.97, -4.74) * mm});
            skArc(sketch, "E44", {"start": v(-23.12, 7.1) * mm, "mid": v(-32.25, 4.39) * mm, "end": v(-34.97, -4.74) * mm, "construction": true});
            skArc(sketch, "E45.0.MirrorCS", {"start": v(-23.48, 6.75) * mm, "mid": v(-26.11, -2.1) * mm, "end": v(-34.97, -4.74) * mm});
            skArc(sketch, "E46", {"start": v(11.5, 11.5) * mm, "mid": v(4.37, 9.6) * mm, "end": v(0.24, 3.51) * mm});
            skCircle(sketch, "E47", {"center": v(0, 0) * mm, "radius": 14 * mm});
            skArc(sketch, "E48.MirrorCS", {"start": v(11.5, 11.5) * mm, "mid": v(9.6, 4.37) * mm, "end": v(3.51, 0.24) * mm});
            skArc(sketch, "E49.1.0", {"start": v(-11.5, 11.5) * mm, "mid": v(-9.6, 4.37) * mm, "end": v(-3.51, 0.24) * mm});
            skArc(sketch, "E49.1.1", {"start": v(-11.5, 11.5) * mm, "mid": v(-4.37, 9.6) * mm, "end": v(-0.24, 3.51) * mm});
            skArc(sketch, "E49.2.0", {"start": v(-11.5, -11.5) * mm, "mid": v(-4.37, -9.6) * mm, "end": v(-0.24, -3.51) * mm});
            skArc(sketch, "E49.2.1", {"start": v(-11.5, -11.5) * mm, "mid": v(-9.6, -4.37) * mm, "end": v(-3.51, -0.24) * mm});
            skArc(sketch, "E49.3.0", {"start": v(11.5, -11.5) * mm, "mid": v(9.6, -4.37) * mm, "end": v(3.51, -0.24) * mm});
            skArc(sketch, "E49.3.1", {"start": v(11.5, -11.5) * mm, "mid": v(4.37, -9.6) * mm, "end": v(0.24, -3.51) * mm});
            skArc(sketch, "E50.filletArc", {"start": v(-0.24, 3.51) * mm, "mid": v(0, 3.32) * mm, "end": v(0.24, 3.51) * mm});
            skArc(sketch, "E51.filletArc", {"start": v(3.51, 0.24) * mm, "mid": v(3.32, 0) * mm, "end": v(3.51, -0.24) * mm});
            skArc(sketch, "E52.filletArc", {"start": v(0.24, -3.51) * mm, "mid": v(0, -3.32) * mm, "end": v(-0.24, -3.51) * mm});
            skArc(sketch, "E53.filletArc", {"start": v(-3.51, -0.24) * mm, "mid": v(-3.32, 0) * mm, "end": v(-3.51, 0.24) * mm});
            skSolve(sketch);
        }
        {
            var Q0;
            {var subQ11=sQuery(id+"F15.wireOp",EDGE,"E50.filletArc");Q0=makeQuery(id+"F15.imprint","IMPRINT",FACE,{"disambiguationData":[TD([[makeQuery(id+"F15.imprint","IMPRINT",EDGE,{"derivedFrom":subQ11}),-1.0]])]});}
            extrude(context, id + "F16", {"entities" : qUnion([Q0]), "operationType" : NewBodyOperationType.REMOVE, "oppositeDirection" : true, "depth" : 1.25 * mm});
        }
        {
            var Q0;
            {var subQ0=sQuery(id+"F1.wireOp",EDGE,"E11.0");var subQ1=makeQuery(id+"F14.boolean.opBoolean","COPY",EDGE,{"disambiguationData":[OD(0.0)],"derivedFrom":makeQuery(id+"F14.opExtrude","CAP_EDGE",EDGE,{"disambiguationData":[OSD([subQ0])],"isStart":false})});var subQ3=sQuery(id+"F15.wireOp",EDGE,"E46");Q0=makeQuery(id+"F16.boolean.opBoolean","SPLIT",EDGE,{"disambiguationData":[TD([makeQuery(id+"F16.opExtrude","SWEPT_FACE",FACE,{"disambiguationData":[OSD([subQ3])]})])],"derivedFrom":subQ1});}
            var Q1;
            Q1=makeQuery(id+"F14.boolean.opBoolean","COPY",EDGE,{"derivedFrom":makeQuery(id+"F14.opExtrude","CAP_EDGE",EDGE,{"disambiguationData":[OSD([sQuery(id+"F1.wireOp",EDGE,"E14.0")])],"isStart":false})});
            var Q2;
            {var subQ0=sQuery(id+"F1.wireOp",EDGE,"E11.0");var subQ1=makeQuery(id+"F14.boolean.opBoolean","COPY",EDGE,{"disambiguationData":[OD(0.0)],"derivedFrom":makeQuery(id+"F14.opExtrude","CAP_EDGE",EDGE,{"disambiguationData":[OSD([subQ0])],"isStart":false})});var subQ3=sQuery(id+"F15.wireOp",EDGE,"E49.2.0");Q2=makeQuery(id+"F16.boolean.opBoolean","SPLIT",EDGE,{"disambiguationData":[TD([makeQuery(id+"F16.opExtrude","SWEPT_FACE",FACE,{"disambiguationData":[OSD([subQ3])]})])],"derivedFrom":subQ1});}
            var Q3;
            {var subQ0=sQuery(id+"F1.wireOp",EDGE,"E11.0");var subQ1=makeQuery(id+"F14.boolean.opBoolean","COPY",EDGE,{"disambiguationData":[OD(0.0)],"derivedFrom":makeQuery(id+"F14.opExtrude","CAP_EDGE",EDGE,{"disambiguationData":[OSD([subQ0])],"isStart":false})});var subQ3=sQuery(id+"F15.wireOp",EDGE,"E49.1.0");Q3=makeQuery(id+"F16.boolean.opBoolean","SPLIT",EDGE,{"disambiguationData":[TD([makeQuery(id+"F16.opExtrude","SWEPT_FACE",FACE,{"disambiguationData":[OSD([subQ3])]})])],"derivedFrom":subQ1});}
            fillet(context, id + "F17", {"entities" : qUnion([Q0, Q1, Q2, Q3]), "radius" : .75 * mm, "tangentPropagation" : true, "allowEdgeOverflow" : false});
        }
        {
            var Q0;
            Q0=makeQuery(id+"F16.boolean.opBoolean","COPY",FACE,{"derivedFrom":makeQuery(id+"F16.opExtrude","CAP_FACE",FACE,{"disambiguationData":[OSD([sQuery(id+"F15.wireOp",EDGE,"E46"),sQuery(id+"F15.wireOp",EDGE,"E47"),sQuery(id+"F15.wireOp",EDGE,"E48.MirrorCS"),sQuery(id+"F15.wireOp",EDGE,"E49.1.0"),sQuery(id+"F15.wireOp",EDGE,"E49.1.1"),sQuery(id+"F15.wireOp",EDGE,"E49.2.0"),sQuery(id+"F15.wireOp",EDGE,"E49.2.1"),sQuery(id+"F15.wireOp",EDGE,"E49.3.0"),sQuery(id+"F15.wireOp",EDGE,"E49.3.1"),sQuery(id+"F15.wireOp",EDGE,"E50.filletArc"),sQuery(id+"F15.wireOp",EDGE,"E51.filletArc"),sQuery(id+"F15.wireOp",EDGE,"E52.filletArc"),sQuery(id+"F15.wireOp",EDGE,"E53.filletArc")])],"isStart":false})});
            var sketch = newSketch(context, id + "F18", { "sketchPlane" : qUnion([Q0])});
            skCircle(sketch, "E54", {"center": v(0, 0) * mm, "radius": 1 * mm});
            skSolve(sketch);
        }
        {
            var Q0;
            Q0=qSketchRegion(id+"F18",true);
            extrude(context, id + "F19", {"entities" : qUnion([Q0]), "operationType" : NewBodyOperationType.ADD, "depth" : 1.2 * mm, "hasDraft" : true, "draftAngle" : 10 * degree, "draftPullDirection" : true});
        }
        {
            var Q0;
            {var subQ0=sQuery(id+"F4.wireOp",EDGE,"E20");var subQ1=sQuery(id+"F4.wireOp",EDGE,"E21.0.MirrorCS");var subQ2=sQuery(id+"F6.wireOp",EDGE,"E25");var subQ3=sQuery(id+"F6.wireOp",EDGE,"E27.0.MirrorCS");Q0=makeQuery(id+"F13.opPattern","COPY",EDGE,{"derivedFrom":makeQuery(id+"F10.boolean.opBoolean","INTERSECT",EDGE,{"derivedFrom":[makeQuery(id+"F7.opLoft","SWEPT_FACE",FACE,{"disambiguationData":[OSD([subQ0,subQ1,subQ2,subQ3]),TDD([makeQuery(id+"F4.imprint","INTERSECT",VERTEX,{"disambiguationData":[OD(0.0)],"derivedFrom":[subQ0,subQ1]}),makeQuery(id+"F4.imprint","INTERSECT",VERTEX,{"disambiguationData":[OD(1.0)],"derivedFrom":[subQ0,subQ1]}),makeQuery(id+"F4.imprint","IMPRINT",EDGE,{"derivedFrom":subQ1}),makeQuery(id+"F6.imprint","INTERSECT",VERTEX,{"disambiguationData":[OD(0.0)],"derivedFrom":[subQ2,subQ3]}),makeQuery(id+"F6.imprint","INTERSECT",VERTEX,{"disambiguationData":[OD(1.0)],"derivedFrom":[subQ2,subQ3]}),makeQuery(id+"F6.imprint","IMPRINT",EDGE,{"derivedFrom":subQ3})])]}),makeQuery(id+"F10.opExtrude","SWEPT_FACE",FACE,{"disambiguationData":[OSD([sQuery(id+"F9.wireOp",EDGE,"E29")])]})]}),"instanceName":"3"});}
            var Q1;
            {var subQ0=sQuery(id+"F4.wireOp",EDGE,"E20");var subQ1=sQuery(id+"F4.wireOp",EDGE,"E21.0.MirrorCS");var subQ2=sQuery(id+"F6.wireOp",EDGE,"E25");var subQ3=sQuery(id+"F6.wireOp",EDGE,"E27.0.MirrorCS");Q1=makeQuery(id+"F10.boolean.opBoolean","INTERSECT",EDGE,{"derivedFrom":[makeQuery(id+"F7.opLoft","SWEPT_FACE",FACE,{"disambiguationData":[OSD([subQ0,subQ1,subQ2,subQ3]),TDD([makeQuery(id+"F4.imprint","INTERSECT",VERTEX,{"disambiguationData":[OD(0.0)],"derivedFrom":[subQ0,subQ1]}),makeQuery(id+"F4.imprint","INTERSECT",VERTEX,{"disambiguationData":[OD(1.0)],"derivedFrom":[subQ0,subQ1]}),makeQuery(id+"F4.imprint","IMPRINT",EDGE,{"derivedFrom":subQ1}),makeQuery(id+"F6.imprint","INTERSECT",VERTEX,{"disambiguationData":[OD(0.0)],"derivedFrom":[subQ2,subQ3]}),makeQuery(id+"F6.imprint","INTERSECT",VERTEX,{"disambiguationData":[OD(1.0)],"derivedFrom":[subQ2,subQ3]}),makeQuery(id+"F6.imprint","IMPRINT",EDGE,{"derivedFrom":subQ3})])]}),makeQuery(id+"F10.opExtrude","SWEPT_FACE",FACE,{"disambiguationData":[OSD([sQuery(id+"F9.wireOp",EDGE,"E29")])]})]});}
            var Q2;
            {var subQ0=sQuery(id+"F4.wireOp",EDGE,"E20");var subQ1=sQuery(id+"F4.wireOp",EDGE,"E21.0.MirrorCS");var subQ2=sQuery(id+"F6.wireOp",EDGE,"E25");var subQ3=sQuery(id+"F6.wireOp",EDGE,"E27.0.MirrorCS");Q2=makeQuery(id+"F13.opPattern","COPY",EDGE,{"derivedFrom":makeQuery(id+"F10.boolean.opBoolean","INTERSECT",EDGE,{"derivedFrom":[makeQuery(id+"F7.opLoft","SWEPT_FACE",FACE,{"disambiguationData":[OSD([subQ0,subQ1,subQ2,subQ3]),TDD([makeQuery(id+"F4.imprint","INTERSECT",VERTEX,{"disambiguationData":[OD(0.0)],"derivedFrom":[subQ0,subQ1]}),makeQuery(id+"F4.imprint","INTERSECT",VERTEX,{"disambiguationData":[OD(1.0)],"derivedFrom":[subQ0,subQ1]}),makeQuery(id+"F4.imprint","IMPRINT",EDGE,{"derivedFrom":subQ1}),makeQuery(id+"F6.imprint","INTERSECT",VERTEX,{"disambiguationData":[OD(0.0)],"derivedFrom":[subQ2,subQ3]}),makeQuery(id+"F6.imprint","INTERSECT",VERTEX,{"disambiguationData":[OD(1.0)],"derivedFrom":[subQ2,subQ3]}),makeQuery(id+"F6.imprint","IMPRINT",EDGE,{"derivedFrom":subQ3})])]}),makeQuery(id+"F10.opExtrude","SWEPT_FACE",FACE,{"disambiguationData":[OSD([sQuery(id+"F9.wireOp",EDGE,"E29")])]})]}),"instanceName":"1"});}
            var Q3;
            {var subQ0=sQuery(id+"F4.wireOp",EDGE,"E20");var subQ1=sQuery(id+"F4.wireOp",EDGE,"E21.0.MirrorCS");var subQ2=sQuery(id+"F6.wireOp",EDGE,"E25");var subQ3=sQuery(id+"F6.wireOp",EDGE,"E27.0.MirrorCS");Q3=makeQuery(id+"F13.opPattern","COPY",EDGE,{"derivedFrom":makeQuery(id+"F10.boolean.opBoolean","INTERSECT",EDGE,{"derivedFrom":[makeQuery(id+"F7.opLoft","SWEPT_FACE",FACE,{"disambiguationData":[OSD([subQ0,subQ1,subQ2,subQ3]),TDD([makeQuery(id+"F4.imprint","INTERSECT",VERTEX,{"disambiguationData":[OD(0.0)],"derivedFrom":[subQ0,subQ1]}),makeQuery(id+"F4.imprint","INTERSECT",VERTEX,{"disambiguationData":[OD(1.0)],"derivedFrom":[subQ0,subQ1]}),makeQuery(id+"F4.imprint","IMPRINT",EDGE,{"derivedFrom":subQ1}),makeQuery(id+"F6.imprint","INTERSECT",VERTEX,{"disambiguationData":[OD(0.0)],"derivedFrom":[subQ2,subQ3]}),makeQuery(id+"F6.imprint","INTERSECT",VERTEX,{"disambiguationData":[OD(1.0)],"derivedFrom":[subQ2,subQ3]}),makeQuery(id+"F6.imprint","IMPRINT",EDGE,{"derivedFrom":subQ3})])]}),makeQuery(id+"F10.opExtrude","SWEPT_FACE",FACE,{"disambiguationData":[OSD([sQuery(id+"F9.wireOp",EDGE,"E29")])]})]}),"instanceName":"2"});}
            var Q4;
            Q4=makeQuery(id+"F3.opExtrude","CAP_EDGE",EDGE,{"disambiguationData":[OSD([sQuery(id+"F1.wireOp",EDGE,"E17")])],"isStart":false});
            fillet(context, id + "F20", {"entities" : qUnion([Q0, Q1, Q2, Q3, Q4]), "radius" : .4 * mm, "tangentPropagation" : true, "allowEdgeOverflow" : false});
        }
        {
            var Q0;
            Q0=makeQuery(id+"F2.opExtrude","CAP_EDGE",EDGE,{"disambiguationData":[OSD([sQuery(id+"F1.wireOp",EDGE,"E17")])],"isStart":false});
            fillet(context, id + "F21", {"entities" : qUnion([Q0]), "radius" : .5 * mm, "tangentPropagation" : true, "allowEdgeOverflow" : false});
        }
    });
